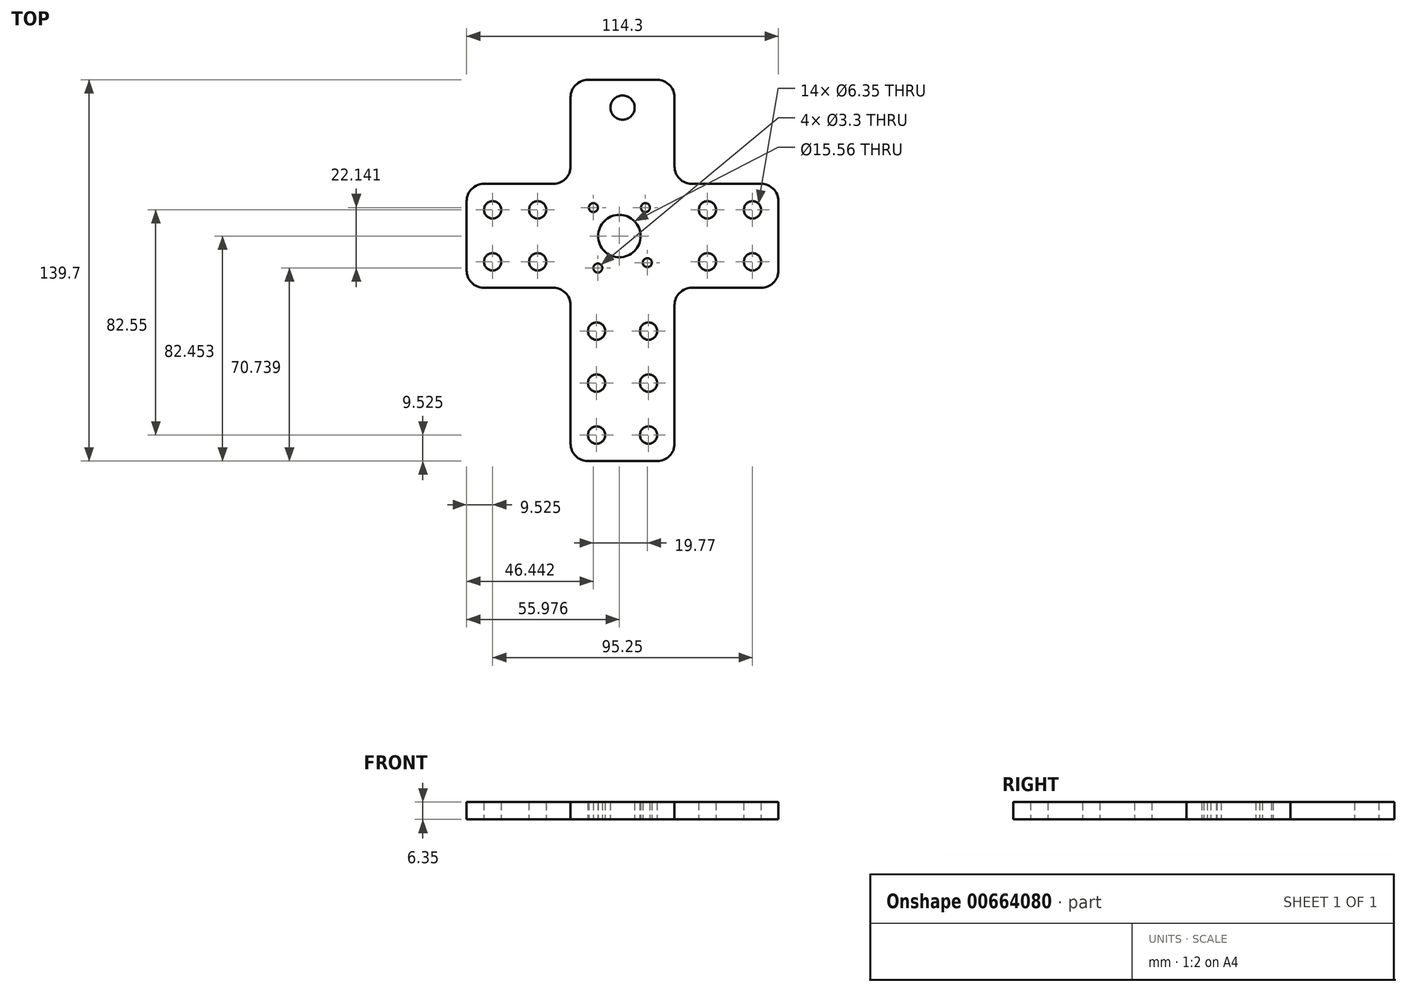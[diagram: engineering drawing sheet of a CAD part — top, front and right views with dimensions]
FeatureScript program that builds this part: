
annotation { "Feature Type Name" : "Feature", "Feature Type Description" : "" }
export const myFeature = defineFeature(function(context is Context, id is Id, definition is map)
    precondition{}
    {
        {
            var Q0;
            Q0=qCreatedBy(makeId("Top.planeOp"),FACE);
            var sketch = newSketch(context, id + "F0", { "sketchPlane" : qUnion([Q0])});
            skLineSegment(sketch, "E0", {"start": v(6.35, 0) * mm, "end": v(31.75, 0) * mm});
            skLineSegment(sketch, "E1", {"start": v(38.1, -6.35) * mm, "end": v(38.1, -31.75) * mm});
            skLineSegment(sketch, "E2", {"start": v(44.45, -38.1) * mm, "end": v(69.85, -38.1) * mm});
            skLineSegment(sketch, "E3", {"start": v(76.2, -44.45) * mm, "end": v(76.2, -69.85) * mm});
            skLineSegment(sketch, "E4", {"start": v(69.85, -76.2) * mm, "end": v(44.45, -76.2) * mm});
            skLineSegment(sketch, "E5", {"start": v(38.1, -82.55) * mm, "end": v(38.1, -133.35) * mm});
            skLineSegment(sketch, "E6", {"start": v(31.75, -139.7) * mm, "end": v(6.35, -139.7) * mm});
            skLineSegment(sketch, "E7", {"start": v(0, -133.35) * mm, "end": v(0, -82.55) * mm});
            skLineSegment(sketch, "E8", {"start": v(-6.35, -76.2) * mm, "end": v(-31.75, -76.2) * mm});
            skLineSegment(sketch, "E9", {"start": v(-38.1, -69.85) * mm, "end": v(-38.1, -44.45) * mm});
            skLineSegment(sketch, "E10", {"start": v(-31.75, -38.1) * mm, "end": v(-6.35, -38.1) * mm});
            skLineSegment(sketch, "E11", {"start": v(0, -31.75) * mm, "end": v(0, -6.35) * mm});
            skCircle(sketch, "E12", {"center": v(9.53, -130.18) * mm, "radius": 3.18 * mm});
            skCircle(sketch, "E13", {"center": v(28.58, -130.18) * mm, "radius": 3.18 * mm});
            skCircle(sketch, "E14", {"center": v(9.53, -111.13) * mm, "radius": 3.18 * mm});
            skCircle(sketch, "E15", {"center": v(28.58, -111.13) * mm, "radius": 3.18 * mm});
            skCircle(sketch, "E16", {"center": v(9.53, -92.08) * mm, "radius": 3.18 * mm});
            skCircle(sketch, "E17", {"center": v(28.57, -92.08) * mm, "radius": 3.18 * mm});
            skCircle(sketch, "E18", {"center": v(-28.57, -47.63) * mm, "radius": 3.18 * mm});
            skCircle(sketch, "E19", {"center": v(-28.57, -66.67) * mm, "radius": 3.18 * mm});
            skCircle(sketch, "E20", {"center": v(-12.06, -47.63) * mm, "radius": 3.18 * mm});
            skCircle(sketch, "E21", {"center": v(-12.06, -66.68) * mm, "radius": 3.18 * mm});
            skLineSegment(sketch, "E22", {"start": v(19.05, 0) * mm, "end": v(19.05, -22.85) * mm, "construction": true});
            skCircle(sketch, "E23.MirrorC", {"center": v(66.68, -47.63) * mm, "radius": 3.18 * mm});
            skCircle(sketch, "E24.MirrorC", {"center": v(50.16, -47.63) * mm, "radius": 3.18 * mm});
            skCircle(sketch, "E25.MirrorC", {"center": v(66.68, -66.67) * mm, "radius": 3.18 * mm});
            skCircle(sketch, "E26.MirrorC", {"center": v(50.16, -66.68) * mm, "radius": 3.18 * mm});
            skCircle(sketch, "E27", {"center": v(17.88, -57.25) * mm, "radius": 7.78 * mm});
            skCircle(sketch, "E28", {"center": v(8.34, -46.82) * mm, "radius": 1.65 * mm});
            skCircle(sketch, "E29", {"center": v(27.4, -46.82) * mm, "radius": 1.65 * mm});
            skCircle(sketch, "E30", {"center": v(28.11, -66.99) * mm, "radius": 1.65 * mm});
            skCircle(sketch, "E31", {"center": v(9.98, -68.96) * mm, "radius": 1.65 * mm});
            skCircle(sketch, "E32", {"center": v(19.05, -10.16) * mm, "radius": 4.45 * mm});
            skPoint(sketch, "E33.visualSharp", {"position": v(0, 0) * mm});
            skArc(sketch, "E33.filletArc", {"start": v(6.35, 0) * mm, "mid": v(1.86, -1.86) * mm, "end": v(0, -6.35) * mm});
            skPoint(sketch, "E34.visualSharp", {"position": v(38.1, 0) * mm});
            skArc(sketch, "E34.filletArc", {"start": v(38.1, -6.35) * mm, "mid": v(36.24, -1.86) * mm, "end": v(31.75, 0) * mm});
            skPoint(sketch, "E35.visualSharp", {"position": v(38.1, -38.1) * mm});
            skArc(sketch, "E35.filletArc", {"start": v(38.1, -31.75) * mm, "mid": v(39.96, -36.24) * mm, "end": v(44.45, -38.1) * mm});
            skPoint(sketch, "E36.visualSharp", {"position": v(76.2, -38.1) * mm});
            skArc(sketch, "E36.filletArc", {"start": v(76.2, -44.45) * mm, "mid": v(74.34, -39.96) * mm, "end": v(69.85, -38.1) * mm});
            skPoint(sketch, "E37.visualSharp", {"position": v(76.2, -76.2) * mm});
            skArc(sketch, "E37.filletArc", {"start": v(69.85, -76.2) * mm, "mid": v(74.34, -74.34) * mm, "end": v(76.2, -69.85) * mm});
            skPoint(sketch, "E38.visualSharp", {"position": v(38.1, -76.2) * mm});
            skArc(sketch, "E38.filletArc", {"start": v(44.45, -76.2) * mm, "mid": v(39.96, -78.06) * mm, "end": v(38.1, -82.55) * mm});
            skPoint(sketch, "E39.visualSharp", {"position": v(38.1, -139.7) * mm});
            skArc(sketch, "E39.filletArc", {"start": v(31.75, -139.7) * mm, "mid": v(36.24, -137.84) * mm, "end": v(38.1, -133.35) * mm});
            skPoint(sketch, "E40.visualSharp", {"position": v(0, -139.7) * mm});
            skArc(sketch, "E40.filletArc", {"start": v(0, -133.35) * mm, "mid": v(1.86, -137.84) * mm, "end": v(6.35, -139.7) * mm});
            skPoint(sketch, "E41.visualSharp", {"position": v(0, -76.2) * mm});
            skArc(sketch, "E41.filletArc", {"start": v(0, -82.55) * mm, "mid": v(-1.86, -78.06) * mm, "end": v(-6.35, -76.2) * mm});
            skPoint(sketch, "E42.visualSharp", {"position": v(-38.1, -76.2) * mm});
            skArc(sketch, "E42.filletArc", {"start": v(-38.1, -69.85) * mm, "mid": v(-36.24, -74.34) * mm, "end": v(-31.75, -76.2) * mm});
            skPoint(sketch, "E43.visualSharp", {"position": v(-38.1, -38.1) * mm});
            skArc(sketch, "E43.filletArc", {"start": v(-31.75, -38.1) * mm, "mid": v(-36.24, -39.96) * mm, "end": v(-38.1, -44.45) * mm});
            skPoint(sketch, "E44.visualSharp", {"position": v(0, -38.1) * mm});
            skArc(sketch, "E44.filletArc", {"start": v(-6.35, -38.1) * mm, "mid": v(-1.86, -36.24) * mm, "end": v(0, -31.75) * mm});
            skLineSegment(sketch, "E45", {"start": v(0, 0) * mm, "end": v(6.35, 0) * mm, "construction": true});
            skSolve(sketch);
        }
        {
            var Q0;
            Q0 = qSketchRegion(id + "F0", true);
            extrude(context, id + "F1", {"entities" : qUnion([Q0]), "depth" : 6.35 * mm, "offsetDistance" : 25.4 * mm});
        }
    });
